# Revit family: Screen_LargeOpening_ExecutiveSeries-Recessed_PhantomScreens-4
name_source: partatom
category: Doors
units: mm (PartAtom-declared; Revit-internal decimal feet)

## family parameters
Always vertical = Yes
Cut with Voids When Loaded = No
Host = Wall
OmniClass Number = 23.30.60.21
OmniClass Title = Insect Screens
Room Calculation Point = No
Shared = No

## types (1)
- Type as Specified
    Analytic Construction = <None>
    Assembly Code = B2020400
    Construction Details = http://www.arcat.com
    Description = Phantom Screens Executive  Series Recessed Screen
    Frame Projection Ext. = 0' - 1"
    Frame Projection Int. = 0' - 1"
    Frame Width = 0' - 3"
    Function = Interior
    Heat Transfer Coefficient (U) = 0.1 BTU/(h·ft²·°F)
    Installation-Fabrication = http://www.phantomscreens.com
    Keynote = 08 11 00
    Manufacturer = Phantom Screens
    Manufacturer Fax = 604-855-7834
    Manufacturer Website = http://www.phantomscreens.com
    Model = Executive  Series Recessed
    Product Data = http://www.arcat.com
    Product Properties = http://www.phantomscreens.com
    Recessed Track = 0' - 1 3/8"
    Recessed Track Width = 0' - 2 1/8"
    Revision = R1_08-2016
    Sales Information = http://www.phantomscreens.com
    Screen = Phifer TuffScreen No-See-Um – Charcoal
    Slide Bar = Dark Acacia
    Slide Bar Height = 0' - 3 11/16"
    Solar Heat Gain Coefficient = 0
    Specification = http://www.phantomscreens.com
    Thermal Resistance (R) = 0.0000 (h·ft²·°F)/BTU
    Track = Dark Acacia
    URL = http://www.phantomscreens.com
    Visual Light Transmittance = 0
    Wall Closure = By host

## geometry (parser evidence)
native form markers: Sweep x3
no freeform markers — native parametric forms only
